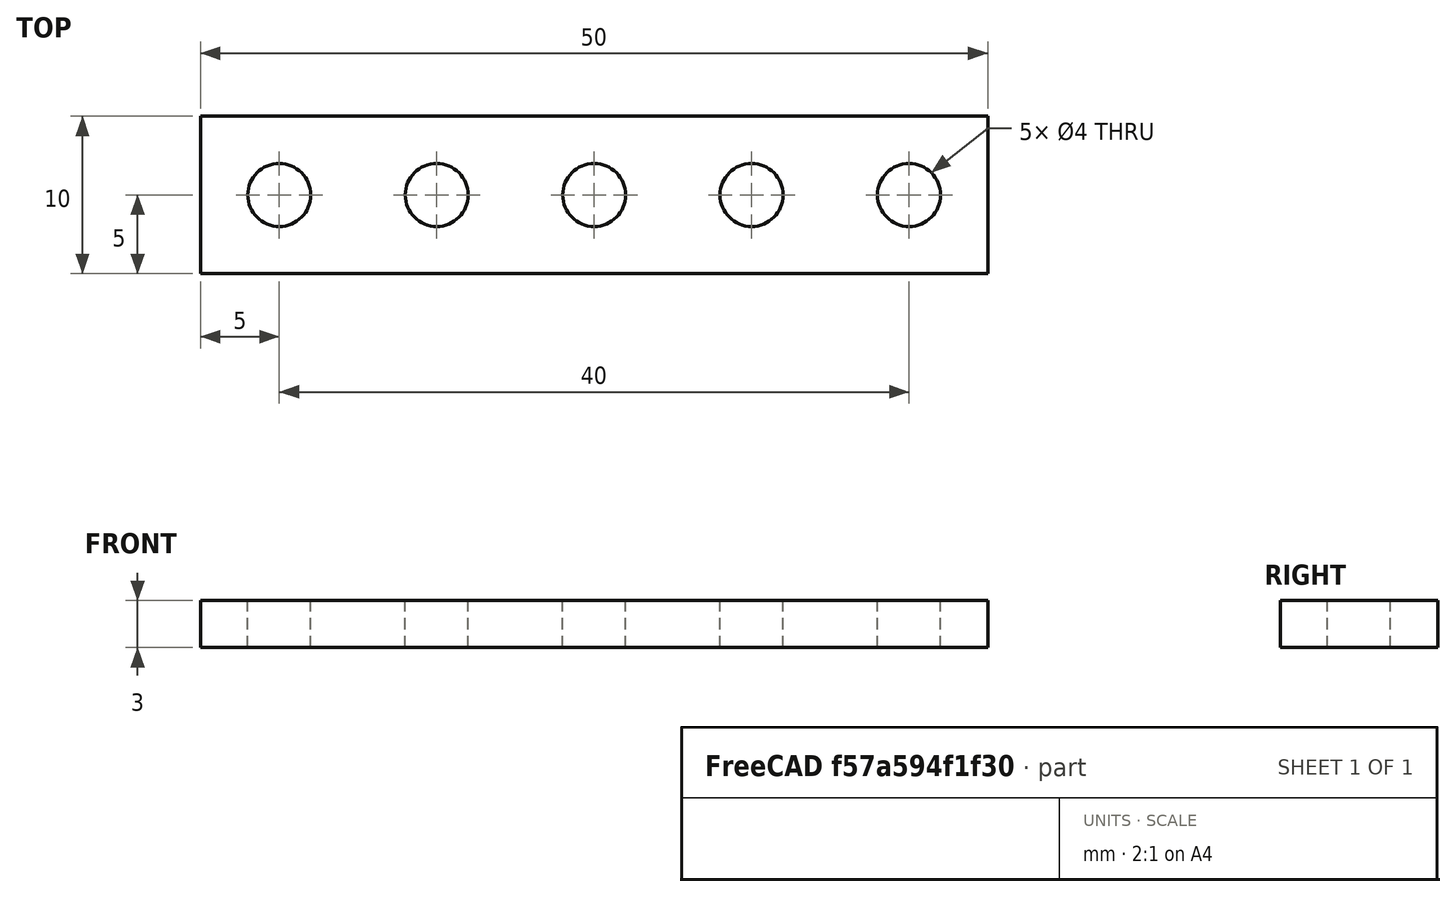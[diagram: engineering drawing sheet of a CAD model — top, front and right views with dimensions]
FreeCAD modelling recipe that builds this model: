
FCSTD DOCUMENT  (FreeCAD 0.19R24291 (Git))
Label: reto3
License: All rights reserved
LicenseURL: http://en.wikipedia.org/wiki/All_rights_reserved
objects: Part::Cylinder×5, App::MeasureDistance×4, Part::Box×1, Part::MultiFuse×1, Part::Cut×1
note: 8 computed .brp shape members not serialized (recipe doc carries the construction recipe); baked Part::Feature solids carry a one-line shape summary decoded from their .brp

FEATURE [Part::Box] Box  label="Cube"
  AttacherType = Attacher::AttachEngine3D
  Height = 3
  Length = 50
  Width = 10
FEATURE [Part::Cylinder] Cylinder
  Angle = 360
  AttacherType = Attacher::AttachEngine3D
  Height = 10
  Placement = pos=(5,5,-3) rot=(0,0,1;0rad)
  Radius = 2
FEATURE [Part::Cylinder] Cylinder001 .. Cylinder004  x4 (patterned run collapsed; names and placements below)
  Angle = 360
  AttacherType = Attacher::AttachEngine3D
  Height = 10
  Radius = 2
  placements: 4 in arithmetic series — first pos=(15,5,-3) rot=(0,0,1;0rad), step (10,0,0), last pos=(45,5,-3) rot=(0,0,1;0rad)
FEATURE [Part::MultiFuse] Fusion
  Refine = true
  Shapes = -> [Cylinder,Cylinder001,Cylinder002,Cylinder003,Cylinder004]
FEATURE [Part::Cut] Cut
  Base = -> Box
  Refine = true
  Tool = -> Fusion
FEATURE [App::MeasureDistance] Distance  label="Distance: 3,00 mm"
  Distance = 3.00055
  P1 = (50,10,0)
  P2 = (50,9.94235,3)
FEATURE [App::MeasureDistance] Distance001  label="Distance: 9,98 mm"
  Distance = 9.98189
  P1 = (0.00969003,0,3)
  P2 = (0.104551,9.98144,3)
FEATURE [App::MeasureDistance] Distance002  label="Distance: 50,00 mm"
  Distance = 50
  P1 = (0,9.92339,3)
  P2 = (50,9.88981,3)
FEATURE [App::MeasureDistance] Distance003  label="Distance: 10,07 mm"
  Distance = 10.0655
  P1 = (3.35284,6.10873,2.17686)
  P2 = (13.4173,6.20215,2.06939)
